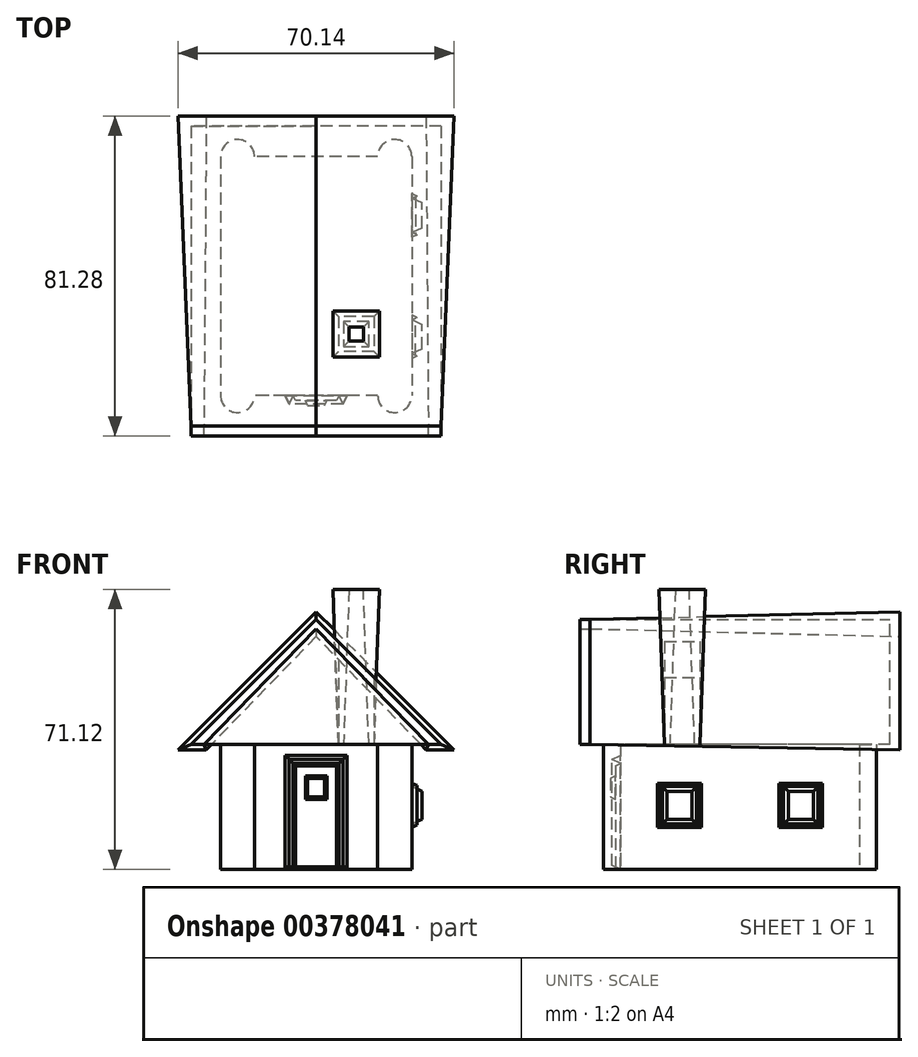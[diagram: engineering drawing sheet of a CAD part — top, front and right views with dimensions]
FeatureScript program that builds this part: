
annotation { "Feature Type Name" : "Feature", "Feature Type Description" : "" }
export const myFeature = defineFeature(function(context is Context, id is Id, definition is map)
    precondition{}
    {
        {
            var Q0;
            Q0=qCreatedBy(makeId("Top.planeOp"),FACE);
            var sketch = newSketch(context, id + "F0", { "sketchPlane" : qUnion([Q0])});
            skLineSegment(sketch, "E0.bottom", {"start": v(24.3, 30.35) * mm, "end": v(-24.3, 30.35) * mm});
            skLineSegment(sketch, "E0.top", {"start": v(24.3, -30.35) * mm, "end": v(-24.3, -30.35) * mm});
            skLineSegment(sketch, "E0.left", {"start": v(24.3, 30.35) * mm, "end": v(24.3, -30.35) * mm});
            skLineSegment(sketch, "E0.right", {"start": v(-24.3, 30.35) * mm, "end": v(-24.3, -30.35) * mm});
            skPoint(sketch, "E0.middle", {"position": v(0, 0) * mm});
            skArc(sketch, "E1", {"start": v(-15.63, 30.35) * mm, "mid": v(-19.97, 34.68) * mm, "end": v(-24.3, 30.35) * mm});
            skArc(sketch, "E2", {"start": v(24.3, 30.35) * mm, "mid": v(19.97, 34.68) * mm, "end": v(15.63, 30.35) * mm});
            skArc(sketch, "E3", {"start": v(-24.3, -30.35) * mm, "mid": v(-19.97, -34.68) * mm, "end": v(-15.63, -30.35) * mm});
            skArc(sketch, "E4", {"start": v(15.63, -30.35) * mm, "mid": v(19.97, -34.68) * mm, "end": v(24.3, -30.35) * mm});
            skLineSegment(sketch, "E5", {"start": v(-24.3, 0) * mm, "end": v(24.3, 0) * mm});
            skLineSegment(sketch, "E6", {"start": v(0, 30.35) * mm, "end": v(0, -30.35) * mm});
            skSolve(sketch);
        }
        {
            var Q0;
            Q0 = qSketchRegion(id + "F0", true);
            extrude(context, id + "F1", {"entities" : qUnion([Q0]), "depth" : 31.75 * mm});
        }
        {
            var Q0;
            Q0=makeQuery(id+"F1.opExtrude","CAP_FACE",FACE,{"disambiguationData":[OSD([sQuery(id+"F0.wireOp",EDGE,"E0.bottom"),sQuery(id+"F0.wireOp",EDGE,"E0.top"),sQuery(id+"F0.wireOp",EDGE,"E0.left"),sQuery(id+"F0.wireOp",EDGE,"E0.right"),sQuery(id+"F0.wireOp",EDGE,"E1"),sQuery(id+"F0.wireOp",EDGE,"E2"),sQuery(id+"F0.wireOp",EDGE,"E3"),sQuery(id+"F0.wireOp",EDGE,"E4")])],"isStart":false});
            var sketch = newSketch(context, id + "F2", { "sketchPlane" : qUnion([Q0])});
            skLineSegment(sketch, "E7.bottom", {"start": v(31.75, 38.1) * mm, "end": v(-31.75, 38.1) * mm});
            skLineSegment(sketch, "E7.top", {"start": v(31.75, -38.1) * mm, "end": v(-31.75, -38.1) * mm});
            skLineSegment(sketch, "E7.left", {"start": v(31.75, 38.1) * mm, "end": v(31.75, -38.1) * mm});
            skLineSegment(sketch, "E7.right", {"start": v(-31.75, 38.1) * mm, "end": v(-31.75, -38.1) * mm});
            skPoint(sketch, "E7.middle", {"position": v(0, 0) * mm});
            skLineSegment(sketch, "E8.bottom", {"start": v(14.7, -10.23) * mm, "end": v(5.63, -10.23) * mm});
            skLineSegment(sketch, "E8.top", {"start": v(14.7, -19.2) * mm, "end": v(5.63, -19.2) * mm});
            skLineSegment(sketch, "E8.left", {"start": v(14.7, -10.23) * mm, "end": v(14.7, -19.2) * mm});
            skLineSegment(sketch, "E8.right", {"start": v(5.63, -10.23) * mm, "end": v(5.63, -19.2) * mm});
            skPoint(sketch, "E8.middle", {"position": v(10.16, -14.71) * mm});
            skLineSegment(sketch, "E9.bottom", {"start": v(13.37, -11.56) * mm, "end": v(6.95, -11.56) * mm});
            skLineSegment(sketch, "E9.top", {"start": v(13.37, -17.86) * mm, "end": v(6.95, -17.86) * mm});
            skLineSegment(sketch, "E9.left", {"start": v(13.37, -11.56) * mm, "end": v(13.37, -17.86) * mm});
            skLineSegment(sketch, "E9.right", {"start": v(6.95, -11.56) * mm, "end": v(6.95, -17.86) * mm});
            skSolve(sketch);
        }
        {
            var Q0;
            Q0=makeQuery(id+"F2.imprint","IMPRINT",FACE,{"disambiguationData":[TD([[makeQuery(id+"F2.imprint","IMPRINT",EDGE,{"derivedFrom":sQuery(id+"F2.wireOp",EDGE,"E7.bottom")}),1.0]])]});
            var Q1;
            Q1=makeQuery(id+"F2.imprint","IMPRINT",FACE,{"disambiguationData":[TD([[makeQuery(id+"F2.imprint","IMPRINT",EDGE,{"derivedFrom":makeQuery(id+"F1.opExtrude","CAP_EDGE",EDGE,{"disambiguationData":[OSD([sQuery(id+"F0.wireOp",EDGE,"E0.bottom")])],"isStart":false})}),1.0]])]});
            extrude(context, id + "F3", {"entities" : qUnion([Q0, Q1]), "depth" : 31.75 * mm});
        }
        {
            var Q0;
            Q0=makeQuery(id+"F3.opExtrude","CAP_EDGE",EDGE,{"disambiguationData":[OSD([sQuery(id+"F2.wireOp",EDGE,"E7.right")])],"isStart":false});
            var Q1;
            Q1=makeQuery(id+"F3.opExtrude","CAP_EDGE",EDGE,{"disambiguationData":[OSD([sQuery(id+"F2.wireOp",EDGE,"E7.left")])],"isStart":false});
            chamfer(context, id + "F4", {"entities" : qUnion([Q0, Q1]), "width" : 31.75 * mm, "tangentPropagation" : true});
        }
        {
            var Q0;
            Q0=makeQuery(id+"F1.opExtrude","SWEPT_FACE",FACE,{"disambiguationData":[OSD([sQuery(id+"F0.wireOp",EDGE,"E0.top")])]});
            var sketch = newSketch(context, id + "F5", { "sketchPlane" : qUnion([Q0])});
            skLineSegment(sketch, "E10.bottom", {"start": v(7.84, 0) * mm, "end": v(-7.84, 0) * mm});
            skLineSegment(sketch, "E10.top", {"start": v(7.84, 29) * mm, "end": v(-7.84, 29) * mm});
            skLineSegment(sketch, "E10.left", {"start": v(7.84, 0) * mm, "end": v(7.84, 29) * mm});
            skLineSegment(sketch, "E10.right", {"start": v(-7.84, 0) * mm, "end": v(-7.84, 29) * mm});
            skPoint(sketch, "E10.middle", {"position": v(0, 14.5) * mm});
            skLineSegment(sketch, "E11.bottom", {"start": v(5.83, 0) * mm, "end": v(-5.83, 0) * mm});
            skLineSegment(sketch, "E11.top", {"start": v(5.83, 26.94) * mm, "end": v(-5.83, 26.94) * mm});
            skLineSegment(sketch, "E11.left", {"start": v(5.83, 0) * mm, "end": v(5.83, 26.94) * mm});
            skLineSegment(sketch, "E11.right", {"start": v(-5.83, 0) * mm, "end": v(-5.83, 26.94) * mm});
            skPoint(sketch, "E11.middle", {"position": v(0, 13.47) * mm});
            skLineSegment(sketch, "E12.bottom", {"start": v(3.32, 24.3) * mm, "end": v(-3.32, 24.3) * mm});
            skLineSegment(sketch, "E12.top", {"start": v(3.32, 17.2) * mm, "end": v(-3.32, 17.2) * mm});
            skLineSegment(sketch, "E12.left", {"start": v(3.32, 24.3) * mm, "end": v(3.32, 17.2) * mm});
            skLineSegment(sketch, "E12.right", {"start": v(-3.32, 24.3) * mm, "end": v(-3.32, 17.2) * mm});
            skPoint(sketch, "E12.middle", {"position": v(0, 20.76) * mm});
            skSolve(sketch);
        }
        {
            var Q0;
            Q0=makeQuery(id+"F5.imprint","IMPRINT",FACE,{"disambiguationData":[TD([[makeQuery(id+"F5.imprint","IMPRINT",EDGE,{"derivedFrom":sQuery(id+"F5.wireOp",EDGE,"E10.top")}),1.0]])]});
            extrude(context, id + "F6", {"entities" : qUnion([Q0]), "operationType" : NewBodyOperationType.ADD, "depth" : 5.08 * mm, "hasDraft" : true, "draftAngle" : 25 * degree, "draftPullDirection" : true});
        }
        {
            var Q0;
            {var subQ1=sQuery(id+"F0.wireOp",EDGE,"E0.top");Q0=makeQuery(id+"F6.boolean.opBoolean","SPLIT",FACE,{"disambiguationData":[TD([makeQuery(id+"F6.opExtrude","SWEPT_FACE",FACE,{"disambiguationData":[OSD([sQuery(id+"F5.wireOp",EDGE,"E11.top")])]})])],"derivedFrom":makeQuery(id+"F1.opExtrude","SWEPT_FACE",FACE,{"disambiguationData":[OSD([subQ1])]})});}
            extrude(context, id + "F7", {"entities" : qUnion([Q0]), "operationType" : NewBodyOperationType.ADD, "depth" : 1.27 * mm, "hasDraft" : true, "draftAngle" : 25 * degree, "draftPullDirection" : true});
        }
        {
            var Q0;
            Q0=makeQuery(id+"F5.imprint","IMPRINT",FACE,{"disambiguationData":[TD([[makeQuery(id+"F5.imprint","IMPRINT",EDGE,{"derivedFrom":sQuery(id+"F5.wireOp",EDGE,"E12.bottom")}),1.0]])]});
            extrude(context, id + "F8", {"entities" : qUnion([Q0]), "operationType" : NewBodyOperationType.ADD, "depth" : 2.54 * mm, "hasDraft" : true, "draftAngle" : 25 * degree, "draftPullDirection" : true});
        }
        {
            var Q0;
            Q0=makeQuery(id+"F1.opExtrude","SWEPT_FACE",FACE,{"disambiguationData":[OSD([sQuery(id+"F0.wireOp",EDGE,"E0.left")])]});
            var sketch = newSketch(context, id + "F9", { "sketchPlane" : qUnion([Q0])});
            skLineSegment(sketch, "E13", {"start": v(0, 0) * mm, "end": v(0, 30.54) * mm});
            skPoint(sketch, "E13.endSnap0", {"position": v(0, 0) * mm});
            skLineSegment(sketch, "E14.bottom", {"start": v(-9.88, 21.9) * mm, "end": v(-20.96, 21.9) * mm});
            skLineSegment(sketch, "E14.top", {"start": v(-9.88, 10.71) * mm, "end": v(-20.96, 10.71) * mm});
            skLineSegment(sketch, "E14.left", {"start": v(-9.88, 21.9) * mm, "end": v(-9.88, 10.71) * mm});
            skLineSegment(sketch, "E14.right", {"start": v(-20.96, 21.9) * mm, "end": v(-20.96, 10.71) * mm});
            skPoint(sketch, "E14.middle", {"position": v(-15.42, 16.3) * mm});
            skLineSegment(sketch, "E15.bottom", {"start": v(20.96, 21.9) * mm, "end": v(9.88, 21.9) * mm});
            skLineSegment(sketch, "E15.top", {"start": v(20.96, 10.71) * mm, "end": v(9.88, 10.71) * mm});
            skLineSegment(sketch, "E15.left", {"start": v(9.88, 21.9) * mm, "end": v(9.88, 10.71) * mm});
            skLineSegment(sketch, "E15.right", {"start": v(20.96, 21.9) * mm, "end": v(20.96, 10.71) * mm});
            skPoint(sketch, "E15.middle", {"position": v(15.42, 16.3) * mm});
            skLineSegment(sketch, "E16.bottom", {"start": v(-11.1, 21.06) * mm, "end": v(-19.74, 21.06) * mm});
            skLineSegment(sketch, "E16.top", {"start": v(-11.1, 11.55) * mm, "end": v(-19.74, 11.55) * mm});
            skLineSegment(sketch, "E16.left", {"start": v(-11.1, 21.06) * mm, "end": v(-11.1, 11.55) * mm});
            skLineSegment(sketch, "E16.right", {"start": v(-19.74, 21.06) * mm, "end": v(-19.74, 11.55) * mm});
            skLineSegment(sketch, "E17.bottom", {"start": v(19.79, 21.05) * mm, "end": v(11.05, 21.05) * mm});
            skLineSegment(sketch, "E17.top", {"start": v(19.79, 11.57) * mm, "end": v(11.05, 11.57) * mm});
            skLineSegment(sketch, "E17.left", {"start": v(19.79, 21.05) * mm, "end": v(19.79, 11.57) * mm});
            skLineSegment(sketch, "E17.right", {"start": v(11.05, 21.05) * mm, "end": v(11.05, 11.57) * mm});
            skSolve(sketch);
        }
        {
            var Q0;
            Q0=makeQuery(id+"F9.imprint","IMPRINT",FACE,{"disambiguationData":[TD([[makeQuery(id+"F9.imprint","IMPRINT",EDGE,{"derivedFrom":sQuery(id+"F9.wireOp",EDGE,"E14.bottom")}),1.0]])]});
            var Q1;
            Q1=makeQuery(id+"F9.imprint","IMPRINT",FACE,{"disambiguationData":[TD([[makeQuery(id+"F9.imprint","IMPRINT",EDGE,{"derivedFrom":sQuery(id+"F9.wireOp",EDGE,"E15.bottom")}),1.0]])]});
            extrude(context, id + "F10", {"entities" : qUnion([Q0, Q1]), "operationType" : NewBodyOperationType.ADD, "depth" : 5.08 * mm, "hasDraft" : true, "draftAngle" : 25 * degree, "draftPullDirection" : true});
        }
        {
            var Q0;
            Q0=makeQuery(id+"F10.boolean.opBoolean","SPLIT",FACE,{"disambiguationData":[TD([makeQuery(id+"F10.opExtrude","SWEPT_FACE",FACE,{"disambiguationData":[OSD([sQuery(id+"F9.wireOp",EDGE,"E16.bottom")])]})])],"derivedFrom":makeQuery(id+"F1.opExtrude","SWEPT_FACE",FACE,{"disambiguationData":[OSD([sQuery(id+"F0.wireOp",EDGE,"E0.left")])]})});
            var Q1;
            Q1=makeQuery(id+"F10.boolean.opBoolean","SPLIT",FACE,{"disambiguationData":[TD([makeQuery(id+"F10.opExtrude","SWEPT_FACE",FACE,{"disambiguationData":[OSD([sQuery(id+"F9.wireOp",EDGE,"E17.bottom")])]})])],"derivedFrom":makeQuery(id+"F1.opExtrude","SWEPT_FACE",FACE,{"disambiguationData":[OSD([sQuery(id+"F0.wireOp",EDGE,"E0.left")])]})});
            extrude(context, id + "F11", {"entities" : qUnion([Q0, Q1]), "operationType" : NewBodyOperationType.ADD, "depth" : 2.54 * mm, "hasDraft" : true, "draftAngle" : 25 * degree, "draftPullDirection" : true});
        }
        {
            var Q0;
            Q0=makeQuery(id+"F3.opExtrude","SWEPT_FACE",FACE,{"disambiguationData":[OSD([sQuery(id+"F2.wireOp",EDGE,"E7.top")])]});
            var sketch = newSketch(context, id + "F12", { "sketchPlane" : qUnion([Q0])});
            skLineSegment(sketch, "E18", {"start": v(-28.5, 31.75) * mm, "end": v(0, 61.14) * mm});
            skLineSegment(sketch, "E19", {"start": v(0, 61.14) * mm, "end": v(28.5, 31.75) * mm});
            skLineSegment(sketch, "E20", {"start": v(28.5, 31.75) * mm, "end": v(31.75, 31.75) * mm});
            skLineSegment(sketch, "E21", {"start": v(31.75, 31.75) * mm, "end": v(0, 63.5) * mm});
            skLineSegment(sketch, "E22", {"start": v(0, 63.5) * mm, "end": v(-31.75, 31.75) * mm});
            skLineSegment(sketch, "E23", {"start": v(-31.75, 31.75) * mm, "end": v(-28.5, 31.75) * mm});
            skLineSegment(sketch, "E24", {"start": v(0, 61.14) * mm, "end": v(0, 31.75) * mm});
            skSolve(sketch);
        }
        {
            var Q0;
            Q0=makeQuery(id+"F12.imprint","IMPRINT",FACE,{"disambiguationData":[TD([[makeQuery(id+"F12.imprint","IMPRINT",EDGE,{"derivedFrom":sQuery(id+"F12.wireOp",EDGE,"E18")}),1.0]])]});
            extrude(context, id + "F13", {"entities" : qUnion([Q0]), "depth" : 2.54 * mm, "hasSecondDirection" : true, "secondDirectionOppositeDirection" : true, "secondDirectionDepth" : 78.74 * mm, "hasSecondDirectionDraft" : true, "secondDirectionDraftAngle" : 1 * degree});
        }
        {
            var Q0;
            Q0=makeQuery(id+"F2.imprint","IMPRINT",FACE,{"disambiguationData":[TD([[makeQuery(id+"F2.imprint","IMPRINT",EDGE,{"derivedFrom":sQuery(id+"F2.wireOp",EDGE,"E8.bottom")}),1.0]])]});
            extrude(context, id + "F14", {"entities" : qUnion([Q0]), "depth" : 39.37 * mm, "hasDraft" : true, "draftAngle" : 2 * degree});
        }
    });
